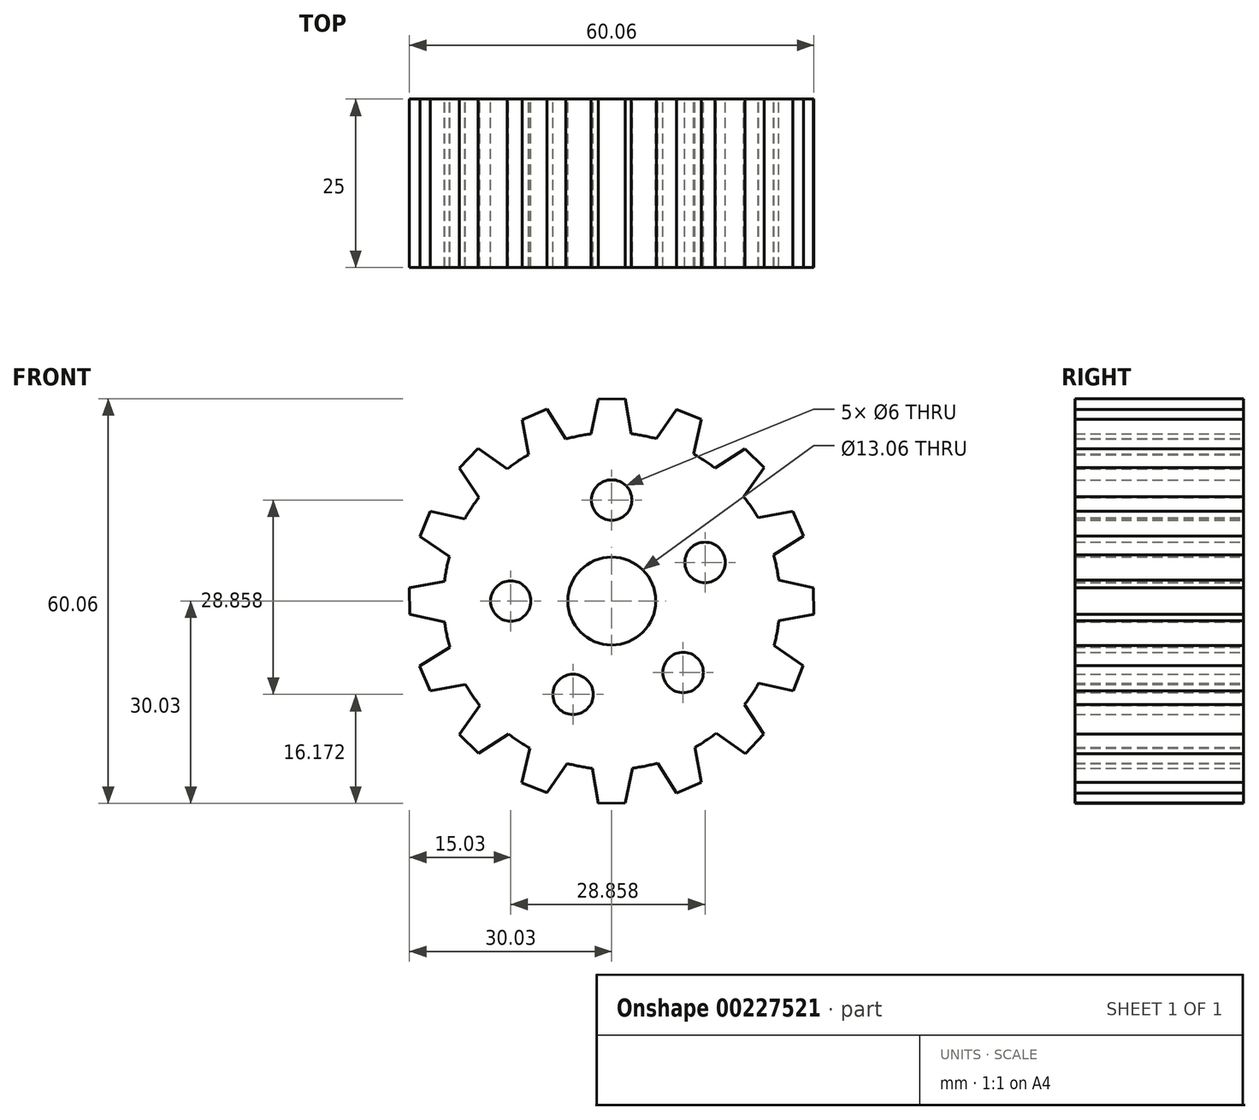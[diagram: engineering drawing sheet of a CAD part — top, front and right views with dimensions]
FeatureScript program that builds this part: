
annotation { "Feature Type Name" : "Feature", "Feature Type Description" : "" }
export const myFeature = defineFeature(function(context is Context, id is Id, definition is map)
    precondition{}
    {
        {
            var Q0;
            Q0=qCreatedBy(makeId("Front.planeOp"),FACE);
            var sketch = newSketch(context, id + "F0", { "sketchPlane" : qUnion([Q0])});
            skCircle(sketch, "E0", {"center": v(0, 0) * mm, "radius": 6.53 * mm});
            skCircle(sketch, "E1", {"center": v(0, 0) * mm, "radius": 25 * mm});
            skCircle(sketch, "E2", {"center": v(0, 0) * mm, "radius": 15 * mm, "construction": true});
            skLineSegment(sketch, "E3", {"start": v(-2, 29.97) * mm, "end": v(-3.1, 24.8) * mm});
            skLineSegment(sketch, "E4", {"start": v(2, 30.03) * mm, "end": v(2.9, 24.83) * mm});
            skLineSegment(sketch, "E5", {"start": v(-2, 29.97) * mm, "end": v(2, 30.03) * mm});
            skPoint(sketch, "E6", {"position": v(0, 30) * mm});
            skPoint(sketch, "E7", {"position": v(0, 15) * mm});
            skCircle(sketch, "E8", {"center": v(0, 15) * mm, "radius": 3 * mm});
            skCircle(sketch, "E9.1.0", {"center": v(13.86, 5.74) * mm, "radius": 3 * mm});
            skCircle(sketch, "E9.2.0", {"center": v(10.6, -10.6) * mm, "radius": 3 * mm});
            skCircle(sketch, "E9.3.0", {"center": v(-5.74, -13.86) * mm, "radius": 3 * mm});
            skCircle(sketch, "E9.4.0", {"center": v(-15, 0) * mm, "radius": 3 * mm});
            skLineSegment(sketch, "E9.anchor1", {"start": v(0, 0) * mm, "end": v(0, 15) * mm, "construction": true});
            skLineSegment(sketch, "E9.anchor2", {"start": v(0, 0) * mm, "end": v(-15, 0) * mm, "construction": true});
            skLineSegment(sketch, "E10.1.0", {"start": v(-13.31, 26.92) * mm, "end": v(-12.36, 21.73) * mm});
            skLineSegment(sketch, "E10.1.1", {"start": v(-13.31, 26.92) * mm, "end": v(-9.64, 28.5) * mm});
            skLineSegment(sketch, "E10.1.2", {"start": v(-9.64, 28.5) * mm, "end": v(-6.83, 24.05) * mm});
            skLineSegment(sketch, "E10.2.0", {"start": v(-22.6, 19.77) * mm, "end": v(-19.74, 15.35) * mm});
            skLineSegment(sketch, "E10.2.1", {"start": v(-22.6, 19.77) * mm, "end": v(-19.82, 22.65) * mm});
            skLineSegment(sketch, "E10.2.2", {"start": v(-19.82, 22.65) * mm, "end": v(-15.51, 19.6) * mm});
            skLineSegment(sketch, "E10.3.0", {"start": v(-28.45, 9.62) * mm, "end": v(-24.1, 6.62) * mm});
            skLineSegment(sketch, "E10.3.1", {"start": v(-28.45, 9.62) * mm, "end": v(-26.98, 13.34) * mm});
            skLineSegment(sketch, "E10.3.2", {"start": v(-26.98, 13.34) * mm, "end": v(-21.83, 12.18) * mm});
            skLineSegment(sketch, "E10.4.0", {"start": v(-29.97, -2) * mm, "end": v(-24.8, -3.1) * mm});
            skLineSegment(sketch, "E10.4.1", {"start": v(-29.97, -2) * mm, "end": v(-30.03, 2) * mm});
            skLineSegment(sketch, "E10.4.2", {"start": v(-30.03, 2) * mm, "end": v(-24.83, 2.9) * mm});
            skLineSegment(sketch, "E10.5.0", {"start": v(-26.92, -13.31) * mm, "end": v(-21.73, -12.36) * mm});
            skLineSegment(sketch, "E10.5.1", {"start": v(-26.92, -13.31) * mm, "end": v(-28.5, -9.64) * mm});
            skLineSegment(sketch, "E10.5.2", {"start": v(-28.5, -9.64) * mm, "end": v(-24.05, -6.83) * mm});
            skLineSegment(sketch, "E10.6.0", {"start": v(-19.77, -22.6) * mm, "end": v(-15.35, -19.74) * mm});
            skLineSegment(sketch, "E10.6.1", {"start": v(-19.77, -22.6) * mm, "end": v(-22.65, -19.82) * mm});
            skLineSegment(sketch, "E10.6.2", {"start": v(-22.65, -19.82) * mm, "end": v(-19.6, -15.51) * mm});
            skLineSegment(sketch, "E10.7.0", {"start": v(-9.62, -28.45) * mm, "end": v(-6.62, -24.1) * mm});
            skLineSegment(sketch, "E10.7.1", {"start": v(-9.62, -28.45) * mm, "end": v(-13.34, -26.98) * mm});
            skLineSegment(sketch, "E10.7.2", {"start": v(-13.34, -26.98) * mm, "end": v(-12.18, -21.83) * mm});
            skLineSegment(sketch, "E10.8.0", {"start": v(2, -29.97) * mm, "end": v(3.1, -24.8) * mm});
            skLineSegment(sketch, "E10.8.1", {"start": v(2, -29.97) * mm, "end": v(-2, -30.03) * mm});
            skLineSegment(sketch, "E10.8.2", {"start": v(-2, -30.03) * mm, "end": v(-2.9, -24.83) * mm});
            skLineSegment(sketch, "E10.9.0", {"start": v(13.31, -26.92) * mm, "end": v(12.36, -21.73) * mm});
            skLineSegment(sketch, "E10.9.1", {"start": v(13.31, -26.92) * mm, "end": v(9.64, -28.5) * mm});
            skLineSegment(sketch, "E10.9.2", {"start": v(9.64, -28.5) * mm, "end": v(6.83, -24.05) * mm});
            skLineSegment(sketch, "E10.10.0", {"start": v(22.6, -19.77) * mm, "end": v(19.74, -15.35) * mm});
            skLineSegment(sketch, "E10.10.1", {"start": v(22.6, -19.77) * mm, "end": v(19.82, -22.65) * mm});
            skLineSegment(sketch, "E10.10.2", {"start": v(19.82, -22.65) * mm, "end": v(15.51, -19.6) * mm});
            skLineSegment(sketch, "E10.11.0", {"start": v(28.45, -9.62) * mm, "end": v(24.1, -6.62) * mm});
            skLineSegment(sketch, "E10.11.1", {"start": v(28.45, -9.62) * mm, "end": v(26.98, -13.34) * mm});
            skLineSegment(sketch, "E10.11.2", {"start": v(26.98, -13.34) * mm, "end": v(21.83, -12.18) * mm});
            skLineSegment(sketch, "E10.12.0", {"start": v(29.97, 2) * mm, "end": v(24.8, 3.1) * mm});
            skLineSegment(sketch, "E10.12.1", {"start": v(29.97, 2) * mm, "end": v(30.03, -2) * mm});
            skLineSegment(sketch, "E10.12.2", {"start": v(30.03, -2) * mm, "end": v(24.83, -2.9) * mm});
            skLineSegment(sketch, "E10.13.0", {"start": v(26.92, 13.31) * mm, "end": v(21.73, 12.36) * mm});
            skLineSegment(sketch, "E10.13.1", {"start": v(26.92, 13.31) * mm, "end": v(28.5, 9.64) * mm});
            skLineSegment(sketch, "E10.13.2", {"start": v(28.5, 9.64) * mm, "end": v(24.05, 6.83) * mm});
            skLineSegment(sketch, "E10.14.0", {"start": v(19.77, 22.6) * mm, "end": v(15.35, 19.74) * mm});
            skLineSegment(sketch, "E10.14.1", {"start": v(19.77, 22.6) * mm, "end": v(22.65, 19.82) * mm});
            skLineSegment(sketch, "E10.14.2", {"start": v(22.65, 19.82) * mm, "end": v(19.6, 15.51) * mm});
            skLineSegment(sketch, "E10.15.0", {"start": v(9.62, 28.45) * mm, "end": v(6.62, 24.1) * mm});
            skLineSegment(sketch, "E10.15.1", {"start": v(9.62, 28.45) * mm, "end": v(13.34, 26.98) * mm});
            skLineSegment(sketch, "E10.15.2", {"start": v(13.34, 26.98) * mm, "end": v(12.18, 21.83) * mm});
            skSolve(sketch);
        }
        {
            var Q0;
            Q0 = qSketchRegion(id + "F0", true);
            extrude(context, id + "F1", {"entities" : qUnion([Q0]), "depth" : 25 * mm});
        }
    });
